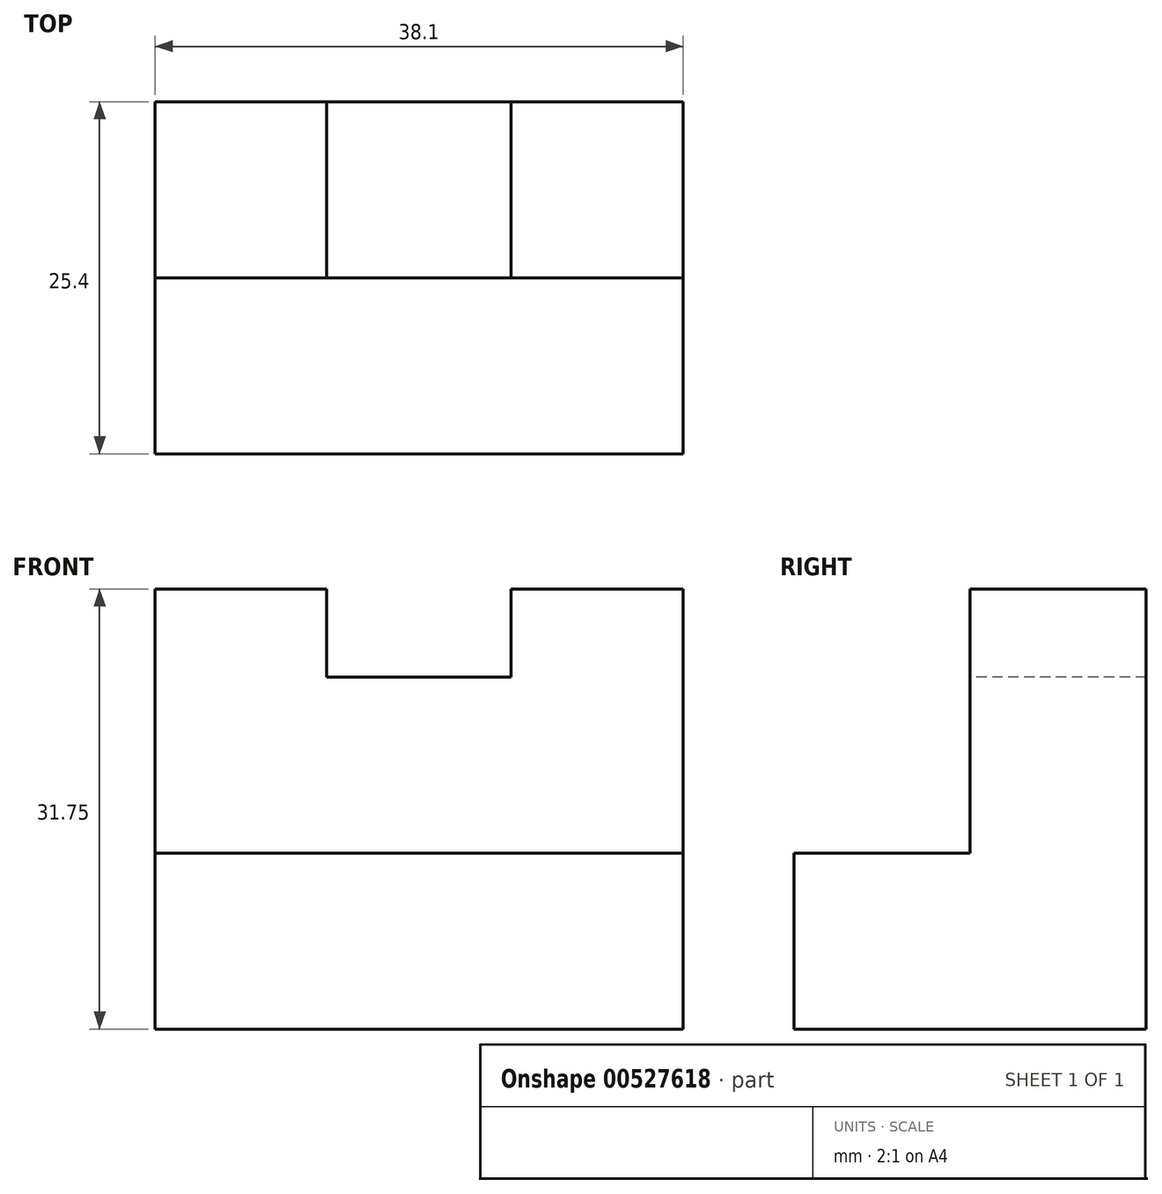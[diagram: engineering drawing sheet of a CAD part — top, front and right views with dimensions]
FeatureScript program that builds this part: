
annotation { "Feature Type Name" : "Feature", "Feature Type Description" : "" }
export const myFeature = defineFeature(function(context is Context, id is Id, definition is map)
    precondition{}
    {
        {
            var Q0;
            Q0=qCreatedBy(makeId("Right.planeOp"),FACE);
            var sketch = newSketch(context, id + "F0", { "sketchPlane" : qUnion([Q0])});
            skLineSegment(sketch, "E0", {"start": v(0, 0) * mm, "end": v(25.4, 0) * mm});
            skLineSegment(sketch, "E1", {"start": v(25.4, 0) * mm, "end": v(25.4, 31.75) * mm});
            skLineSegment(sketch, "E2", {"start": v(25.4, 31.75) * mm, "end": v(12.7, 31.75) * mm});
            skLineSegment(sketch, "E3", {"start": v(12.7, 31.75) * mm, "end": v(12.7, 12.7) * mm});
            skLineSegment(sketch, "E4", {"start": v(12.7, 12.7) * mm, "end": v(0, 12.7) * mm});
            skLineSegment(sketch, "E5", {"start": v(0, 0) * mm, "end": v(0, 12.7) * mm});
            skSolve(sketch);
        }
        {
            var Q0;
            Q0=makeQuery(id+"F0.imprint","IMPRINT",FACE,{"disambiguationData":[TD([[makeQuery(id+"F0.imprint","IMPRINT",EDGE,{"derivedFrom":sQuery(id+"F0.wireOp",EDGE,"E0")}),1.0]])]});
            extrude(context, id + "F1", {"entities" : qUnion([Q0]), "depth" : 38.1 * mm, "offsetDistance" : 25.4 * mm});
        }
        {
            var Q0;
            Q0=makeQuery(id+"F1.opExtrude","SWEPT_FACE",FACE,{"disambiguationData":[OSD([sQuery(id+"F0.wireOp",EDGE,"E2")])]});
            var sketch = newSketch(context, id + "F2", { "sketchPlane" : qUnion([Q0])});
            skLineSegment(sketch, "E6", {"start": v(12.38, 25.4) * mm, "end": v(12.38, 12.7) * mm});
            skLineSegment(sketch, "E7", {"start": v(12.38, 12.7) * mm, "end": v(25.69, 12.7) * mm});
            skLineSegment(sketch, "E8", {"start": v(25.69, 12.7) * mm, "end": v(25.69, 25.4) * mm});
            skLineSegment(sketch, "E9", {"start": v(12.38, 25.4) * mm, "end": v(25.69, 25.4) * mm});
            skLineSegment(sketch, "E10", {"start": v(25.69, 12.7) * mm, "end": v(12.38, 12.7) * mm});
            skSolve(sketch);
        }
        {
            var Q0;
            Q0=makeQuery(id+"F2.imprint","IMPRINT",FACE,{"disambiguationData":[TD([[makeQuery(id+"F2.imprint","IMPRINT",EDGE,{"derivedFrom":sQuery(id+"F2.wireOp",EDGE,"E6")}),1.0]])]});
            extrude(context, id + "F3", {"entities" : qUnion([Q0]), "operationType" : NewBodyOperationType.REMOVE, "oppositeDirection" : true, "depth" : 6.35 * mm, "offsetDistance" : 25.4 * mm});
        }
    });
